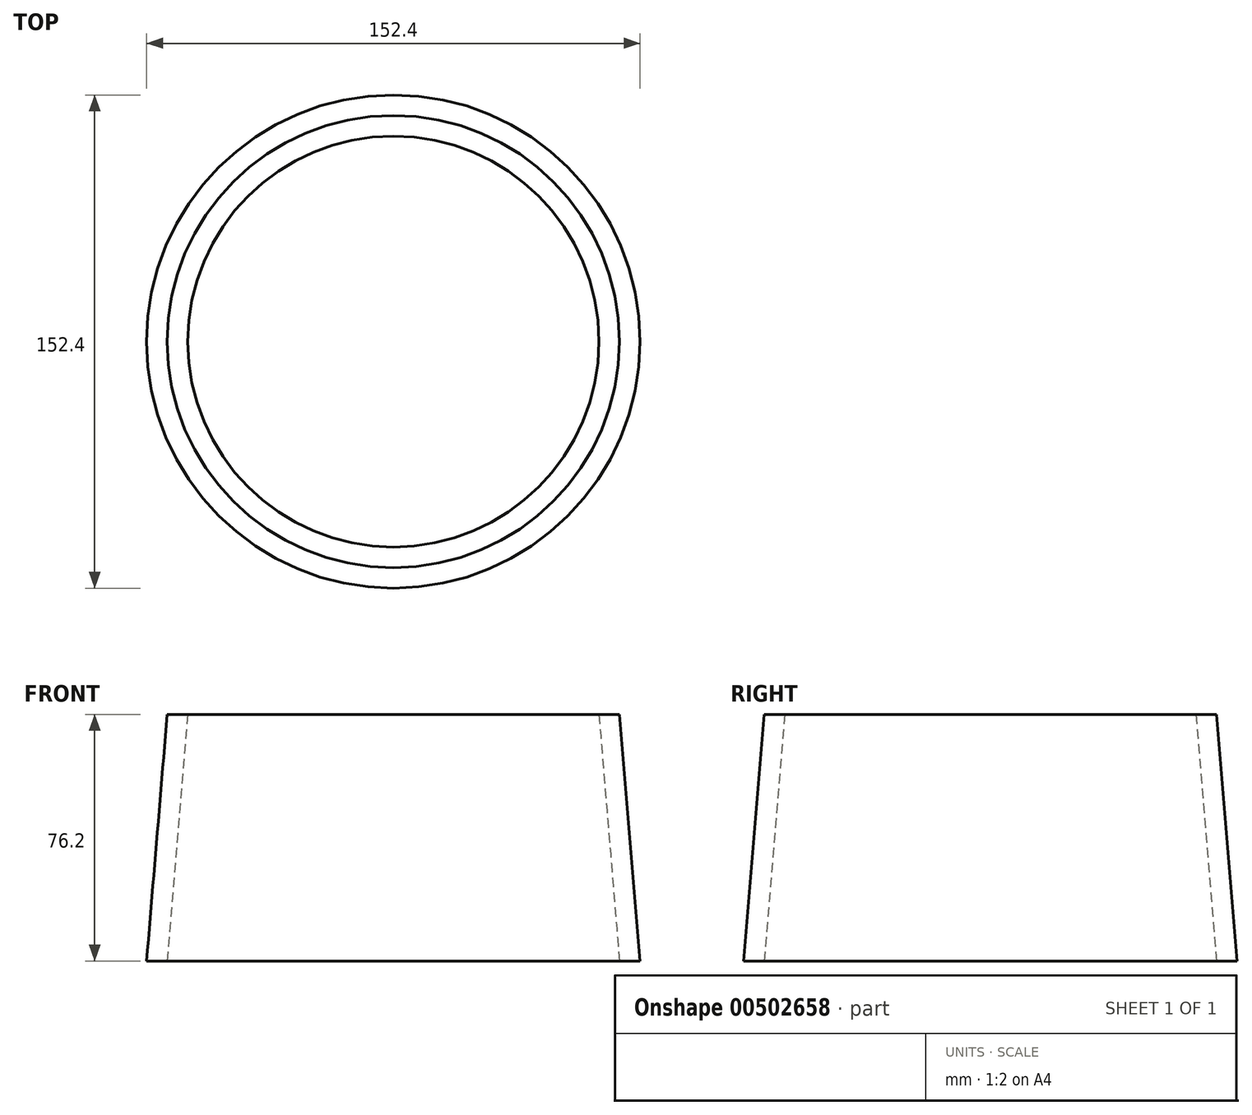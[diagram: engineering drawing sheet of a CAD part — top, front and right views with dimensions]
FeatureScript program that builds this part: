
annotation { "Feature Type Name" : "Feature", "Feature Type Description" : "" }
export const myFeature = defineFeature(function(context is Context, id is Id, definition is map)
    precondition{}
    {
        {
            var Q0;
            Q0=qCreatedBy(makeId("Front.planeOp"),FACE);
            var sketch = newSketch(context, id + "F0", { "sketchPlane" : qUnion([Q0])});
            skLineSegment(sketch, "E0", {"start": v(0, 0) * mm, "end": v(0, 76.2) * mm});
            skLineSegment(sketch, "E1", {"start": v(0, 76.2) * mm, "end": v(-69.85, 76.2) * mm});
            skLineSegment(sketch, "E2", {"start": v(-69.85, 76.2) * mm, "end": v(-76.2, 0) * mm});
            skLineSegment(sketch, "E3", {"start": v(-76.2, 0) * mm, "end": v(0, 0) * mm});
            skSolve(sketch);
        }
        {
            var Q0;
            Q0=makeQuery(id+"F0.imprint","IMPRINT",FACE,{"disambiguationData":[TD([[makeQuery(id+"F0.imprint","IMPRINT",EDGE,{"derivedFrom":sQuery(id+"F0.wireOp",EDGE,"E0")}),1.0]])]});
            var Q1;
            Q1=sQuery(id+"F0.wireOp",EDGE,"E0");
            var Q2;
            Q2=sQuery(id+"F0.wireOp",EDGE,"E0");
            revolve(context, id + "F1", {"entities" : qUnion([Q0]), "surfaceEntities" : qUnion([Q1]), "axis" : qUnion([Q2]), "revolveType" : RevolveType.FULL});
        }
        {
            var Q0;
            Q0=qCreatedBy(makeId("Front.planeOp"),FACE);
            var sketch = newSketch(context, id + "F2", { "sketchPlane" : qUnion([Q0])});
            skLineSegment(sketch, "E4", {"start": v(0, 0) * mm, "end": v(0, 76.2) * mm});
            skLineSegment(sketch, "E5", {"start": v(0, 76.2) * mm, "end": v(63.5, 76.2) * mm});
            skLineSegment(sketch, "E6", {"start": v(63.5, 76.2) * mm, "end": v(69.85, 0) * mm});
            skLineSegment(sketch, "E7", {"start": v(69.85, 0) * mm, "end": v(0, 0) * mm});
            skSolve(sketch);
        }
        {
            var Q0;
            Q0=qSketchRegion(id+"F2",true);
            var Q1;
            Q1=sQuery(id+"F2.wireOp",EDGE,"E4");
            revolve(context, id + "F3", {"operationType" : NewBodyOperationType.REMOVE, "entities" : qUnion([Q0]), "axis" : qUnion([Q1]), "revolveType" : RevolveType.FULL, "oppositeDirection" : true});
        }
    });
